# Revit family: EDLR-195-3000-xxx-SMBx
name_source: partatom
category: Leuchten
units: mm (PartAtom-declared; Revit-internal decimal feet)

## family parameters
Basisbauteil = Fläche
Beim Laden mit Abzugskörper schneiden = Ja
Bemaßung runder Anschluss = Durchmesser verwenden
Gemeinsam genutzt = Nein
Lichtquelle = Ja
OmniClass-Nummer = 23.80.70.11
OmniClass-Titel = Luminaries for Internal Lighting
Raumberechnungspunkt = Nein
Teiletyp = Normal

## types (6) — shared parameters
Baugruppenkennzeichen = D5020200
Datei für fotometrisches Netz = EDLR 195_3000-840 SMB.IES
Emissionsform beim Rendern sichtbar = Nein
Farbfilter = 16777215
Farbtemperaturverschiebung bei Dämpfen der Lampe = <Keine Auswahl>
Hersteller = RIDI Leuchten GmbH
Lampe = LED
Neigungswinkel = 90.00°
URL = www.ridi.de
Von Kreisdurchmesser aussenden = 168 mm  [stored 0.551181 ft]
brand = RIDI
conformity mark = CE
electrical safety class = 1
height = 143 mm
ingress protection (IP) code = IP20
length = 195 mm  [stored 0.639764 ft]
nominal frequency = 50-60Hz
nominal voltage = 230
voltage type (AC, DC, UC) = AC
weight = 0.94kg
width = 195 mm  [stored 0.639764 ft]
zero-valued in all types: Vorgabe-Ansicht

## per-type parameters (varying)
| type | Modell | Scheinlast | rated input power |
| EDLR 195/3000-830 SMB | 0321361 | 23 VA | 23 |
| EDLR 195/3000-830 SMB-DALI | 0331361 | 23 VA | 23 |
| EDLR 195/3000-840 SMB | 0321362 | 23 VA | 23 |
| EDLR 195/3000-840 SMB-DALI | 0331362 | 23 VA | 23 |
| EDLR 195/3000-TW-SMB | 0336671 | 22 VA | 22 |
| EDLR 195/3000-TW-SMB-CAS | 0336671//408 | 22 VA | 22 |

note: column(s) folded — value = type name in every type: product name

note: [stored X ft] marks values corroborated as IEEE doubles in the binary element streams (Revit-internal decimal feet)
